# Revit family: Sink-Kitchen-KOHLER-Strive-K-5281_1
name_source: partatom
category: Plumbing Fixtures
revit_build: Autodesk Revit 2015 (Build: 20140606_1530(x64)
units: mm (PartAtom-declared; Revit-internal decimal feet)

## types (1)
- NA-Stainless
    ADA Compliant = No
    Assembly Code = D2010400
    CW Connection = No
    Cold Water Inlet = Cold Water Inlet
    Date Modified = 01/10/2019
    Default Elevation = 36"
    Description = 32 Inch x 18-5/16 Inch x 9-5/16 Inch under-mount double-equal kitchen sink with accessories
    Drain Included = No
    Finish = Kohler-Metal-NA-Stainless
    HW Connection = No
    Height = 9 5/16"
    Hot Water Inlet = Hot Water Inlet
    Length = 32"
    Manufacturer = KOHLER Co.
    MasterFormat 1995 = 15410
    MasterFormat 2004 = 22.41.16
    Material = 16-Gauge Stainless Steel
    Model = K-5281-NA
    Product Documentation Link = http://www.us.kohler.com
    Product Name = Strive
    Product Page URL = http://www.us.kohler.com
    URL = https://www.us.kohler.com
    Vent Connection = No
    Waste Connection = Yes
    Waste Water Outlet = Waste Water Outlet 2
    Waste Water Outlet 1 = Waste Water Outlet 1
    Width = 18 5/16"

## geometry (parser evidence)
native form markers: Sweep x5
no freeform markers — native parametric forms only
